# Revit family: RLA24
name_source: partatom
category: Lighting Fixtures
revit_build: Autodesk Revit Architecture 2012 (Build: 20110309_2315(x64)
units: mm (PartAtom-declared; Revit-internal decimal feet)

## types (4) — shared parameters
Apparent Load = 0 VA
Backbox = White
Color Filter = 16777215
Default Elevation = 4' - 0"
Description = An architectural style luminaire with four LED color choices, four lumen packages per size, and five driver options
Dimming Lamp Color Temperature Shift = <None>
Driver = 0-10V Dimming
Emit from Line Length = 2' - 0"
Glass = White Glass
Lamp = LED Lamp
Manufacturer = Columbia Lighting
Manufacturer Fax = (866)-898-1065
Model = RLA24
Product Documentation Link = http://www.columbialighting.com
Product Page URL = http://www.columbialighting.com
Row Length = 4' - 0"
Tilt Angle = -90.00°
URL = http://www.columbialighting.com
Voltage = 120 V
Wattage Comments = Up to 95 lumens per watt

## per-type parameters (varying)
| type | Lumen Output | Nominal Watts | Photometric Web File |
| RLA24-30HL-EDU | High Lumen | 55 W | 15.00301.ies |
| RLA24-30LW-EDU | Low Watt | 42 W | 15.00216.ies |
| RLA24-30ML-EDU | Medium Lumen | 52 W | 15.00217.ies |
| RLA24-30VL-EDU | Very High Lumen | 77 W | 15.00302.ies |

## geometry (parser evidence)
native form markers: Sweep x4
no freeform markers — native parametric forms only
